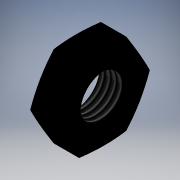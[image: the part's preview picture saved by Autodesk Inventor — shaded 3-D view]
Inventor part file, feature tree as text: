
AUTODESK INVENTOR PART (.ipt)
format: ipt  version: 2017.3 (Build 213256000, 256)  size: 124,416 bytes
history: native  units: mm (DEFAULTED — no unit token found)
features: other x7, sketch x2, revolve x1, thread x1, extrude x1
ambient origin geometry x8: Origin, YZ Plane, XZ Plane, XY Plane, X Axis, Y Axis, Z Axis, Center Point
bodies: Solid1 (feature_tree)
feature tree (12):
  revolve  "Revolution1"  [1 undecoded]
  thread  "Thread1"  [1 undecoded]
  extrude  "Extrusion1"  [1 undecoded]
  other  "NUT_ROD_XY"
  other  "NUT_ROD_YZ"
  other  "NUT_ROD_ZX"
  other  "NUT_ROD_X"
  other  "NUT_ROD_Y"
  other  "NUT_ROD_Z"
  other  "NUT_ROD_Center"
  sketch  "Sketch_1"  dims[d0=360.0deg d1=4.647mm d2=0.0mm d3=12.0mm d4=0.0mm]
  sketch  "Sketch_2"
note: 3 required parameter values undecoded (feature->parameter linkage not recoverable at this tier; creation-order binding heuristic only, values carry confidence <= 0.55)